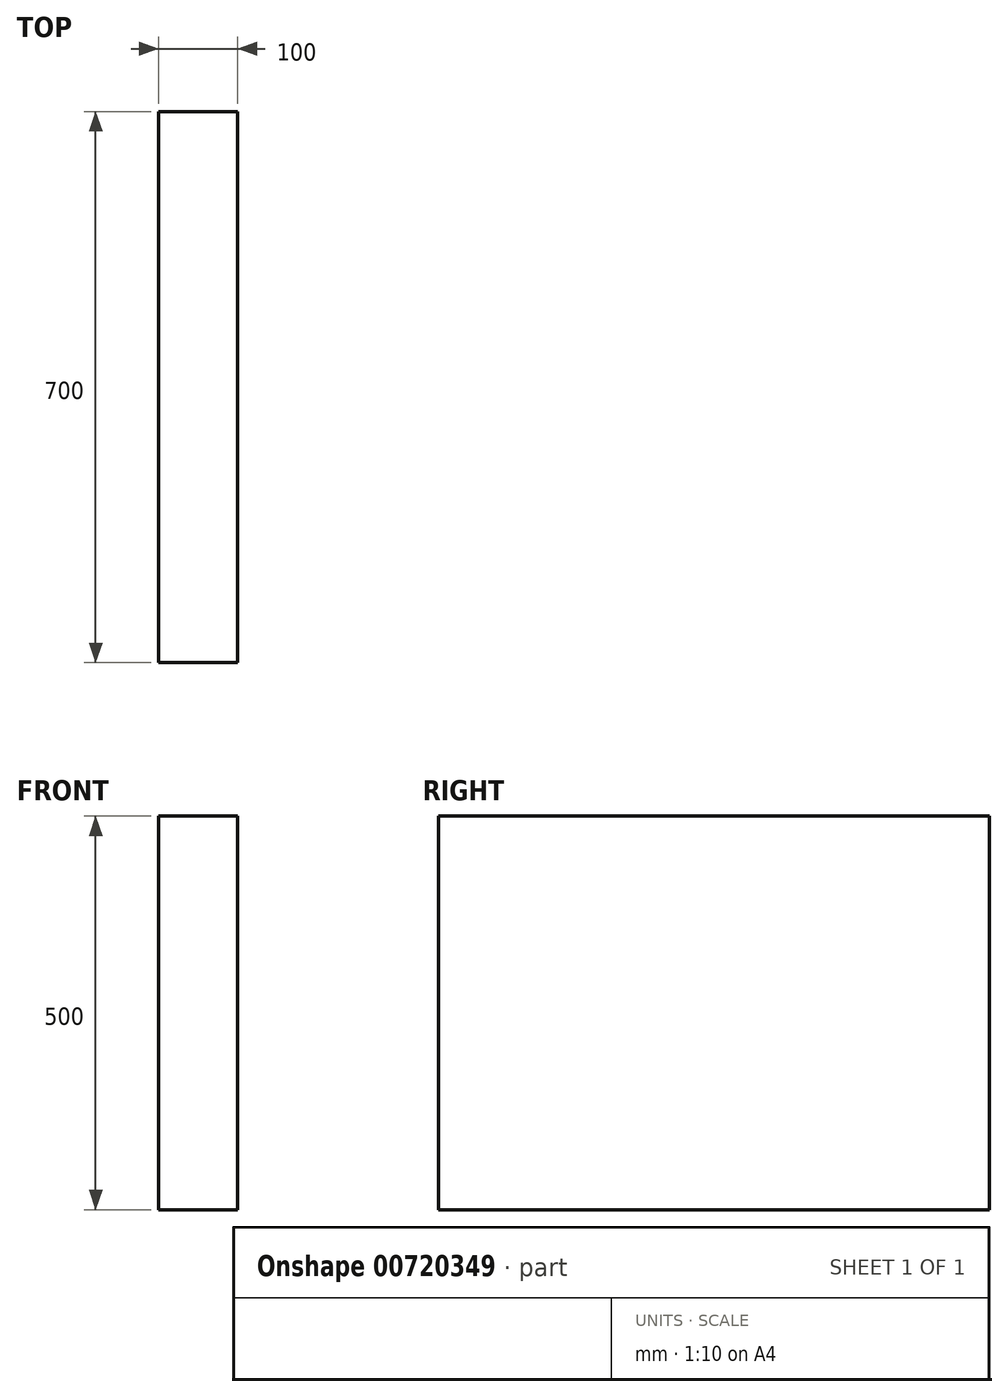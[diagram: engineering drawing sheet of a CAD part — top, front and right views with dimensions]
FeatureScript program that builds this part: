
annotation { "Feature Type Name" : "Feature", "Feature Type Description" : "" }
export const myFeature = defineFeature(function(context is Context, id is Id, definition is map)
    precondition{}
    {
        {
            var Q0;
            Q0=qCreatedBy(makeId("Front.planeOp"),FACE);
            var sketch = newSketch(context, id + "F0", { "sketchPlane" : qUnion([Q0])});
            skLineSegment(sketch, "E0.bottom", {"start": v(0, 0) * mm, "end": v(-100, 0) * mm});
            skLineSegment(sketch, "E0.top", {"start": v(0, -500) * mm, "end": v(-100, -500) * mm});
            skLineSegment(sketch, "E0.left", {"start": v(0, 0) * mm, "end": v(0, -500) * mm});
            skLineSegment(sketch, "E0.right", {"start": v(-100, 0) * mm, "end": v(-100, -500) * mm});
            skSolve(sketch);
        }
        {
            var Q0;
            Q0 = qSketchRegion(id + "F0", true);
            extrude(context, id + "F1", {"entities" : qUnion([Q0]), "depth" : 700 * mm, "offsetDistance" : 25 * mm});
        }
    });
